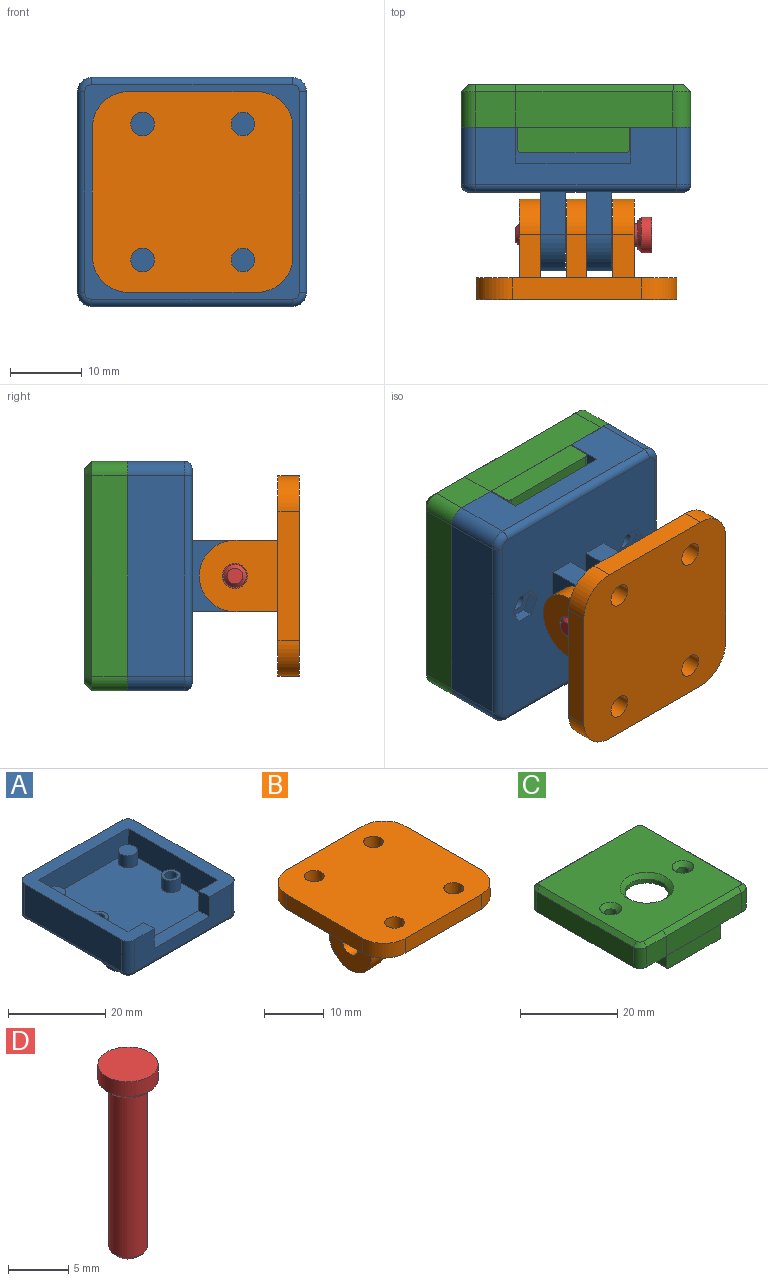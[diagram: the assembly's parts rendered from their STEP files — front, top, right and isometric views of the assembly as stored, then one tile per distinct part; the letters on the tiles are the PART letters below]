
ASSEMBLY  parts=4 mates=3
PART A: 62 faces, bbox 32.3x32.3x20 mm
  f0: plane 30x30mm, normal (0,0,-1), area 800mm2, adj f28,f29,f30,f31,f32,f33,f34,f35
  f1: cylinder r=1.25mm len=4.5mm, axis (0,0,-1), area 35.3mm2, adj f14,f61
  f2: cylinder r=1.25mm len=4.5mm, axis (0,0,-1), area 35.3mm2, adj f16,f54
  f3: plane 32x32mm, normal (0,0,1), area 296.6mm2, adj f4,f6,f7,f8,f9,f10,f11,f12
  f4: plane 28x8mm, normal (0,-1,0), area 144mm2, adj f3,f21,f22,f23,f26,f27,f44
  f5: plane 26x26mm, normal (0,0,1), area 625.7mm2, adj f6,f7,f8,f9,f13,f15,f17,f19
  f6: plane 26x6mm, normal (0,-1,0), area 156mm2, adj f3,f5,f7,f9
  f7: plane 26x6mm, normal (1,0,0), area 156mm2, adj f3,f5,f6,f8
  f8: plane 26x6mm, normal (0,1,0), area 76mm2, adj f3,f5,f7,f9,f21,f22,f23
  f9: plane 26x6mm, normal (-1,0,0), area 156mm2, adj f3,f5,f6,f8
  f10: plane 28x8mm, normal (1,0,0), area 224mm2, adj f3,f24,f27,f40
  f11: plane 28x8mm, normal (0,1,0), area 224mm2, adj f3,f24,f25,f43
  f12: plane 28x8mm, normal (-1,0,0), area 224mm2, adj f3,f25,f26,f47
  f13: cylinder r=2mm len=4mm, axis (0,0,-1), area 37.7mm2, adj f5,f14
  f14: plane 4x4mm, normal (0,0,1), area 7.7mm2, adj f1,f13
  f15: cylinder r=2mm len=4mm, axis (0,0,-1), area 37.7mm2, adj f5,f16
  f16: plane 4x4mm, normal (0,0,1), area 7.7mm2, adj f2,f15
  f17: cylinder r=2mm len=4mm, axis (0,0,-1), area 37.7mm2, adj f5,f18
  f18: plane 4x4mm, normal (0,0,1), area 12.6mm2, adj f17
  f19: cylinder r=2mm len=4mm, axis (0,0,-1), area 37.7mm2, adj f5,f20
  f20: plane 4x4mm, normal (0,0,1), area 12.6mm2, adj f19
  f21: plane 5x3mm, normal (1,0,0), area 15mm2, adj f3,f4,f8,f22
  f22: plane 16x3mm, normal (0,0,1), area 48mm2, adj f4,f8,f21,f23
  f23: plane 5x3mm, normal (-1,0,0), area 15mm2, adj f3,f4,f8,f22
  f24: cylinder r=2mm len=8mm, axis (0,0,-1), area 25.1mm2, adj f3,f10,f11,f41
  f25: cylinder r=2mm len=8mm, axis (0,0,1), area 25.1mm2, adj f3,f11,f12,f45
  f26: cylinder r=2mm len=8mm, axis (0,0,-1), area 25.1mm2, adj f3,f4,f12,f46
  f27: cylinder r=2mm len=8mm, axis (0,0,1), area 25.1mm2, adj f3,f4,f10,f42
  f28: plane 11x10mm, normal (1,0,0), area 86.7mm2, adj f0,f29,f31,f37,f39
  f29: plane 6x3.5mm, normal (0,1,0), area 21mm2, adj f0,f28,f30,f37
  f30: plane 11x10mm, normal (-1,0,0), area 86.7mm2, adj f0,f29,f31,f37,f39
  f31: plane 6x3.5mm, normal (0,-1,0), area 21mm2, adj f0,f28,f30,f37
  f32: plane 11x10mm, normal (1,0,0), area 86.7mm2, adj f0,f33,f35,f36,f38
  f33: plane 6x3.5mm, normal (0,1,0), area 21mm2, adj f0,f32,f34,f36
  f34: plane 11x10mm, normal (-1,0,0), area 86.7mm2, adj f0,f33,f35,f36,f38
  f35: plane 6x3.5mm, normal (0,-1,0), area 21mm2, adj f0,f32,f34,f36
  f36: cylinder r=5mm len=10mm, axis (-1,0,0), area 55mm2, adj f32,f33,f34,f35
  f37: cylinder r=5mm len=10mm, axis (-1,0,0), area 55mm2, adj f28,f29,f30,f31
  f38: cylinder r=2mm len=4mm, axis (1,0,0), area 44mm2, adj f32,f34
  f39: cylinder r=2mm len=4mm, axis (1,0,0), area 44mm2, adj f28,f30
  f40: cylinder r=1mm len=28mm, axis (0,1,0), area 44mm2, adj f0,f10,f41,f42
  f41: torus R=1mm, axis (0,0,1), area 4mm2, adj f0,f24,f40,f43
  f42: torus R=1mm, axis (0,0,1), area 4mm2, adj f0,f27,f40,f44
  f43: cylinder r=1mm len=28mm, axis (-1,0,0), area 44mm2, adj f0,f11,f41,f45
  f44: cylinder r=1mm len=28mm, axis (1,0,0), area 44mm2, adj f0,f4,f42,f46
  f45: torus R=1mm, axis (0,0,1), area 4mm2, adj f0,f25,f43,f47
  f46: torus R=1mm, axis (0,0,1), area 4mm2, adj f0,f26,f44,f47
  f47: cylinder r=1mm len=28mm, axis (0,-1,0), area 44mm2, adj f0,f12,f45,f46
  f48: plane 2.37x1.5mm, normal (0,1,0), area 3.6mm2, adj f0,f49,f53,f54
  f49: plane 2.05x1.5mm, normal (0.87,0.5,0), area 3.6mm2, adj f0,f48,f50,f54
  f50: plane 2.05x1.5mm, normal (0.87,-0.5,0), area 3.6mm2, adj f0,f49,f51,f54
  f51: plane 2.37x1.5mm, normal (0,-1,0), area 3.6mm2, adj f0,f50,f52,f54
  f52: plane 2.05x1.5mm, normal (-0.87,-0.5,0), area 3.6mm2, adj f0,f51,f53,f54
  f53: plane 2.05x1.5mm, normal (-0.87,0.5,0), area 3.6mm2, adj f0,f48,f52,f54
  f54: plane 4.73x4.1mm, normal (0,0,-1), area 9.6mm2, adj f2,f48,f49,f50,f51,f52,f53
  f55: plane 2.37x1.5mm, normal (0,1,0), area 3.6mm2, adj f0,f56,f60,f61
  f56: plane 2.05x1.5mm, normal (0.87,0.5,0), area 3.6mm2, adj f0,f55,f57,f61
  f57: plane 2.05x1.5mm, normal (0.87,-0.5,0), area 3.6mm2, adj f0,f56,f58,f61
  f58: plane 2.37x1.5mm, normal (0,-1,0), area 3.6mm2, adj f0,f57,f59,f61
  f59: plane 2.05x1.5mm, normal (-0.87,-0.5,0), area 3.6mm2, adj f0,f58,f60,f61
  f60: plane 2.05x1.5mm, normal (-0.87,0.5,0), area 3.6mm2, adj f0,f55,f59,f61
  f61: plane 4.73x4.1mm, normal (0,0,-1), area 9.6mm2, adj f1,f55,f56,f57,f58,f59,f60
PART B: 32 faces, bbox 28x28x14 mm
  f0: plane 18x3mm, normal (0,-1,0), area 54mm2, adj f4,f5,f28,f31
  f1: plane 18x3mm, normal (1,0,0), area 54mm2, adj f4,f5,f28,f29
  f2: plane 18x3mm, normal (0,1,0), area 54mm2, adj f4,f5,f29,f30
  f3: plane 18x3mm, normal (-1,0,0), area 54mm2, adj f4,f5,f30,f31
  f4: plane 28x28mm, normal (0,0,-1), area 640.3mm2, adj f0,f1,f2,f3,f6,f7,f8,f9
  f5: plane 28x28mm, normal (0,0,1), area 728.3mm2, adj f0,f1,f2,f3,f24,f25,f26,f27
  f6: plane 6x2.8mm, normal (0,-1,0), area 16.8mm2, adj f4,f7,f9,f19
  f7: plane 11x10mm, normal (-1,0,0), area 89.6mm2, adj f4,f6,f8,f19,f23
  f8: plane 6x2.8mm, normal (0,1,0), area 16.8mm2, adj f4,f7,f9,f19
  f9: plane 11x10mm, normal (1,0,0), area 89.6mm2, adj f4,f6,f8,f19,f23
  f10: plane 11x10mm, normal (1,0,0), area 89.6mm2, adj f4,f11,f13,f20,f22
  f11: plane 6x3mm, normal (0,-1,0), area 18mm2, adj f4,f10,f12,f20
  f12: plane 11x10mm, normal (-1,0,0), area 89.6mm2, adj f4,f11,f13,f20,f22
  f13: plane 6x3mm, normal (0,1,0), area 18mm2, adj f4,f10,f12,f20
  f14: plane 6x3mm, normal (0,-1,0), area 18mm2, adj f4,f15,f17,f18
  f15: plane 11x10mm, normal (-1,0,0), area 89.6mm2, adj f4,f14,f16,f18,f21
  f16: plane 6x3mm, normal (0,1,0), area 18mm2, adj f4,f15,f17,f18
  f17: plane 11x10mm, normal (1,0,0), area 89.6mm2, adj f4,f14,f16,f18,f21
  f18: cylinder r=5mm len=10mm, axis (1,0,0), area 47.1mm2, adj f14,f15,f16,f17
  f19: cylinder r=5mm len=10mm, axis (1,0,0), area 44mm2, adj f6,f7,f8,f9
  f20: cylinder r=5mm len=10mm, axis (-1,0,0), area 47.1mm2, adj f10,f11,f12,f13
  f21: cylinder r=1.75mm len=3.5mm, axis (1,0,0), area 33mm2, adj f15,f17
  f22: cylinder r=1.75mm len=3.5mm, axis (1,0,0), area 33mm2, adj f10,f12
  f23: cylinder r=1.75mm len=3.5mm, axis (1,0,0), area 30.8mm2, adj f7,f9
  f24: cylinder r=1.65mm len=3.3mm, axis (0,0,-1), area 31.1mm2, adj f4,f5
  f25: cylinder r=1.65mm len=3.3mm, axis (0,0,-1), area 31.1mm2, adj f4,f5
  f26: cylinder r=1.65mm len=3.3mm, axis (0,0,-1), area 31.1mm2, adj f4,f5
  f27: cylinder r=1.65mm len=3.3mm, axis (0,0,-1), area 31.1mm2, adj f4,f5
  f28: cylinder r=5mm len=5mm, axis (0,0,-1), area 23.6mm2, adj f0,f1,f4,f5
  f29: cylinder r=5mm len=5mm, axis (0,0,1), area 23.6mm2, adj f1,f2,f4,f5
  f30: cylinder r=5mm len=5mm, axis (0,0,-1), area 23.6mm2, adj f2,f3,f4,f5
  f31: cylinder r=5mm len=5mm, axis (0,0,1), area 23.6mm2, adj f0,f3,f4,f5
PART C: 48 faces, bbox 32x32x9.5 mm
  f0: cylinder r=4.5mm len=9mm, axis (0,0,1), area 28.3mm2, adj f28,f40
  f1: plane 26x26mm, normal (0,0,-1), area 398.8mm2, adj f3,f4,f5,f14,f17,f20,f23,f25
  f2: plane 30x30mm, normal (0,0,1), area 771.6mm2, adj f29,f30,f31,f32,f33,f34,f35,f36
  f3: plane 26x3mm, normal (0,-1,0), area 78mm2, adj f1,f4,f5,f16
  f4: plane 26x3mm, normal (1,0,0), area 78mm2, adj f1,f3,f14,f16
  f5: plane 26x3mm, normal (-1,0,0), area 78mm2, adj f1,f3,f14,f16
  f6: plane 28x5mm, normal (1,0,0), area 140mm2, adj f7,f15,f16,f35
  f7: cylinder r=2mm len=5mm, axis (0,0,1), area 15.7mm2, adj f6,f8,f16,f33
  f8: plane 28x5mm, normal (0,1,0), area 140mm2, adj f7,f9,f16,f31
  f9: cylinder r=2mm len=5mm, axis (0,0,1), area 15.7mm2, adj f8,f10,f16,f32
  f10: plane 28x5mm, normal (-1,0,0), area 140mm2, adj f9,f11,f16,f34
  f11: cylinder r=2mm len=5mm, axis (0,0,1), area 15.7mm2, adj f10,f12,f16,f36
  f12: plane 5.6x5mm, normal (0,-1,0), area 28mm2, adj f11,f13,f16,f38
  f13: plane 21.92x5mm, normal (0,-1,0), area 109.6mm2, adj f12,f15,f16,f39,f41
  f14: plane 26x6.5mm, normal (0,1,0), area 132.8mm2, adj f1,f4,f5,f16,f43,f44,f45,f46
  f15: cylinder r=2mm len=5mm, axis (0,0,1), area 18.2mm2, adj f6,f13,f16,f37
  f16: plane 32x32mm, normal (0,0,-1), area 297.1mm2, adj f3,f4,f5,f6,f7,f8,f9,f10
  f17: cylinder r=2mm len=5mm, axis (0,0,1), area 62.8mm2, adj f1,f19
  f18: cylinder r=1.25mm len=7mm, axis (0,0,1), area 55mm2, adj f19,f30
  f19: plane 4x4mm, normal (0,0,-1), area 7.7mm2, adj f17,f18
  f20: cylinder r=2mm len=5mm, axis (0,0,1), area 62.8mm2, adj f1,f22
  f21: cylinder r=1.25mm len=7mm, axis (0,0,1), area 55mm2, adj f22,f29
  f22: plane 4x4mm, normal (0,0,-1), area 7.7mm2, adj f20,f21
  f23: cylinder r=2mm len=5mm, axis (0,0,1), area 62.8mm2, adj f1,f24
  f24: plane 4x4mm, normal (0,0,-1), area 12.6mm2, adj f23
  f25: cylinder r=2mm len=5mm, axis (0,0,1), area 62.8mm2, adj f1,f26
  f26: plane 4x4mm, normal (0,0,-1), area 12.6mm2, adj f25
  f27: cylinder r=8.5mm len=17mm, axis (0,0,-1), area 53.4mm2, adj f1,f28
  f28: plane 17x17mm, normal (0,0,-1), area 163.4mm2, adj f0,f27
  f29: cone r=1.25mm half-angle=45deg, axis (0,0,1), area 15.6mm2, adj f2,f21
  f30: cone r=1.25mm half-angle=45deg, axis (0,0,1), area 15.6mm2, adj f2,f18
  f31: plane 28x1mm, normal (0,0.71,0.71), area 39.6mm2, adj f2,f8,f32,f33
  f32: cone r=1mm half-angle=45deg, axis (0,0,-1), area 3.3mm2, adj f2,f9,f31,f34
  f33: cone r=1mm half-angle=45deg, axis (0,0,-1), area 3.3mm2, adj f2,f7,f31,f35
  f34: plane 28x1mm, normal (-0.71,0,0.71), area 39.6mm2, adj f2,f10,f32,f36
  f35: plane 28x1mm, normal (0.71,0,0.71), area 39.6mm2, adj f2,f6,f33,f37
  f36: cone r=1mm half-angle=45deg, axis (0,0,-1), area 3.3mm2, adj f2,f11,f34,f38
  f37: cone r=1mm half-angle=45deg, axis (0,0,-1), area 3.9mm2, adj f2,f15,f35,f39
  f38: plane 5.6x1mm, normal (0,-0.71,0.71), area 7.9mm2, adj f2,f12,f36,f39
  f39: plane 22.1x1.1mm, normal (0,-0.71,0.71), area 31.1mm2, adj f2,f13,f37,f38
  f40: cone r=4.5mm half-angle=45deg, axis (0,0,1), area 44.4mm2, adj f0,f2
  f41: plane 15.7x0.04mm, normal (0,0,1), area 0.3mm2, adj f13,f42,f44
  f42: plane 15.7x3.5mm, normal (0,-1,0), area 54.8mm2, adj f41,f43,f44,f45,f46,f47
  f43: plane 3x3mm, normal (-1,0,0), area 9mm2, adj f14,f16,f42,f47
  f44: plane 3x3mm, normal (1,0,0), area 9mm2, adj f14,f16,f41,f42,f46
  f45: plane 14.7x3mm, normal (0,0,-1), area 44.1mm2, adj f14,f42,f46,f47
  f46: cylinder r=0.5mm len=3mm, axis (0,1,0), area 2.4mm2, adj f14,f42,f44,f45
  f47: cylinder r=0.5mm len=3mm, axis (0,-1,0), area 2.4mm2, adj f14,f42,f43,f45
PART D: 7 faces, bbox 5x5x19 mm
  f0: cylinder r=2.5mm len=5mm, axis (0,0,1), area 23.6mm2, adj f2,f3
  f1: plane 4x4mm, normal (0,0,-1), area 4.5mm2, adj f3,f4
  f2: plane 5x5mm, normal (0,0,1), area 19.6mm2, adj f0
  f3: cone r=2.5mm half-angle=45deg, axis (0,0,1), area 10mm2, adj f0,f1
  f4: cylinder r=1.6mm len=16.5mm, axis (0,0,1), area 165.9mm2, adj f1,f6
  f5: plane 2.2x2.2mm, normal (0,0,-1), area 3.8mm2, adj f6
  f6: cone r=1.1mm half-angle=45deg, axis (0,0,1), area 6mm2, adj f4,f5
PLACE A rot(axis=(-1,0,0),90deg) t=(-15,0,2)mm
PLACE B rot(axis=(1,0,0),90deg) t=(42.27,-15,-12)mm
PLACE C rot(axis=(-1,0,0),90deg) t=(-15,-19,2)mm
PLACE D rot(axis=(0,1,0),90deg) t=(-4.4,14.72,-55.53)mm
MATE fastened C.f16 <-> A.f3  axis (0,1,0) through (-1,9,-14)mm
MATE fastened B.f18 <-> A.f38  axis (1,0,0) through (-13.5,-6,2)mm
MATE pin_slot D.f0 <-> B.f18  axis (-1,0,0) through (-22.9,-6,2)mm
